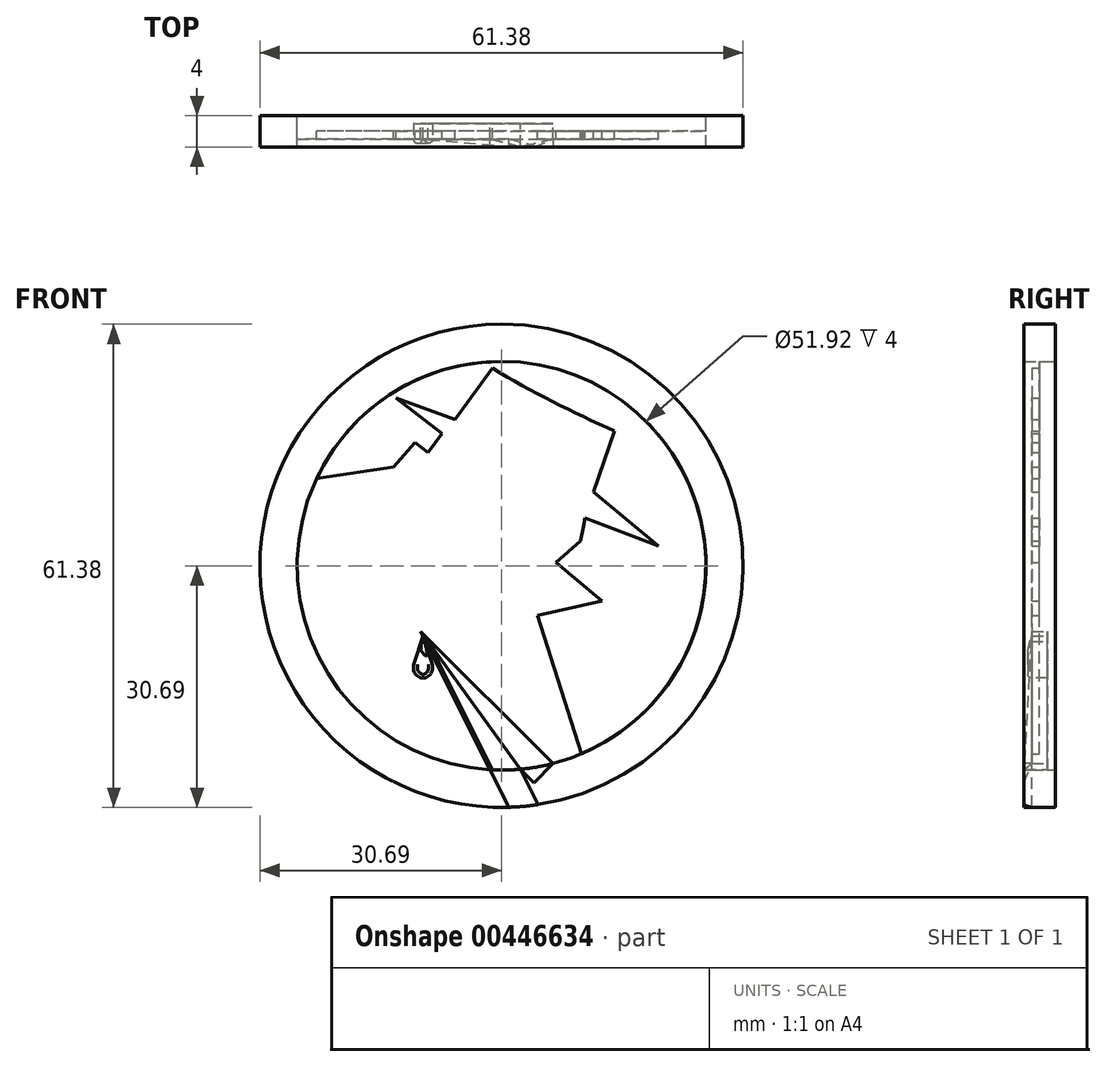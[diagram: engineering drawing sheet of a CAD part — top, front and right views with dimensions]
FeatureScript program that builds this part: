
annotation { "Feature Type Name" : "Feature", "Feature Type Description" : "" }
export const myFeature = defineFeature(function(context is Context, id is Id, definition is map)
    precondition{}
    {
        {
            var Q0;
            Q0=qCreatedBy(makeId("Front.planeOp"),FACE);
            var sketch = newSketch(context, id + "F0", { "sketchPlane" : qUnion([Q0])});
            skLineSegment(sketch, "E0", {"start": v(-50, 0) * mm, "end": v(0, 0) * mm, "construction": true});
            skLineSegment(sketch, "E1", {"start": v(0, 0) * mm, "end": v(50, 0) * mm, "construction": true});
            skCircle(sketch, "E2", {"center": v(-0.5, -1.8) * mm, "radius": 30.7 * mm});
            skCircle(sketch, "E3", {"center": v(-0.5, -1.8) * mm, "radius": 25.96 * mm});
            skLineSegment(sketch, "E4", {"start": v(9.67, -25.69) * mm, "end": v(4.1, -8.1) * mm});
            skLineSegment(sketch, "E5", {"start": v(4.1, -8.1) * mm, "end": v(12.24, -6.27) * mm});
            skLineSegment(sketch, "E6", {"start": v(12.24, -6.27) * mm, "end": v(6.44, -1.37) * mm});
            skLineSegment(sketch, "E7", {"start": v(6.44, -1.37) * mm, "end": v(9.54, 1.38) * mm});
            skLineSegment(sketch, "E8", {"start": v(9.54, 1.38) * mm, "end": v(9.93, 3.2) * mm});
            skLineSegment(sketch, "E9", {"start": v(9.93, 3.2) * mm, "end": v(10.07, 4.26) * mm});
            skLineSegment(sketch, "E10", {"start": v(10.07, 4.26) * mm, "end": v(19.43, 0.68) * mm});
            skLineSegment(sketch, "E11", {"start": v(19.43, 0.68) * mm, "end": v(11.15, 7.54) * mm});
            skLineSegment(sketch, "E12", {"start": v(11.15, 7.54) * mm, "end": v(13.87, 15.33) * mm});
            skLineSegment(sketch, "E13", {"start": v(13.87, 15.33) * mm, "end": v(-1.67, 23.3) * mm, "construction": true});
            skLineSegment(sketch, "E14", {"start": v(-1.67, 23.3) * mm, "end": v(-6.4, 16.78) * mm});
            skLineSegment(sketch, "E15", {"start": v(-6.4, 16.78) * mm, "end": v(-13.93, 19.48) * mm});
            skLineSegment(sketch, "E16", {"start": v(-13.93, 19.48) * mm, "end": v(-8.05, 14.98) * mm});
            skLineSegment(sketch, "E17", {"start": v(-8.05, 14.98) * mm, "end": v(-9.86, 12.61) * mm});
            skLineSegment(sketch, "E18", {"start": v(-9.86, 12.61) * mm, "end": v(-11.49, 13.86) * mm});
            skLineSegment(sketch, "E19", {"start": v(-11.49, 13.86) * mm, "end": v(-14.24, 10.78) * mm});
            skLineSegment(sketch, "E20", {"start": v(-14.24, 10.78) * mm, "end": v(-23.99, 9.26) * mm});
            skArc(sketch, "E21", {"start": v(-1.67, 23.3) * mm, "mid": v(5.97, 19.06) * mm, "end": v(13.87, 15.33) * mm});
            skLineSegment(sketch, "E22", {"start": v(9.99, 3.62) * mm, "end": v(5.75, 4.17) * mm});
            skLineSegment(sketch, "E23", {"start": v(5.75, 4.17) * mm, "end": v(5.75, 1.77) * mm});
            skLineSegment(sketch, "E24", {"start": v(5.75, 1.77) * mm, "end": v(9.86, 2.9) * mm});
            skLineSegment(sketch, "E25", {"start": v(-2.41, 9.54) * mm, "end": v(2.5, 5.2) * mm});
            skLineSegment(sketch, "E26", {"start": v(2.5, 5.2) * mm, "end": v(0.45, 4.05) * mm});
            skLineSegment(sketch, "E27", {"start": v(0.45, 4.05) * mm, "end": v(-2.41, 9.54) * mm});
            skLineSegment(sketch, "E28", {"start": v(6.04, -26.92) * mm, "end": v(-10.78, -10.16) * mm});
            skLineSegment(sketch, "E29", {"start": v(-10.78, -10.16) * mm, "end": v(-1.94, -27.72) * mm});
            skLineSegment(sketch, "E30", {"start": v(1.89, -27.65) * mm, "end": v(-10.78, -10.16) * mm});
            skLineSegment(sketch, "E31", {"start": v(-10.48, -14.68) * mm, "end": v(-10.48, -10.75) * mm, "construction": true});
            skEllipse(sketch, "E32", {"center": v(-10.48, -14.68) * mm, "majorRadius": 1.4 * mm, "minorRadius": 1.23 * mm, "majorAxis": v(0, 1)});
            skLineSegment(sketch, "E33", {"start": v(-11.63, -14.18) * mm, "end": v(-10.48, -10.75) * mm});
            skLineSegment(sketch, "E34", {"start": v(-10.48, -10.75) * mm, "end": v(-9.33, -14.18) * mm});
            skLineSegment(sketch, "E35", {"start": v(-1.65, -27.73) * mm, "end": v(-9.86, -11.42) * mm});
            skLineSegment(sketch, "E36", {"start": v(-1.94, -27.72) * mm, "end": v(7.37, -23.04) * mm, "construction": true});
            skLineSegment(sketch, "E37", {"start": v(6.04, -26.92) * mm, "end": v(-3.22, -36.22) * mm, "construction": true});
            skLineSegment(sketch, "E38", {"start": v(0.6, -25.88) * mm, "end": v(-1.94, -27.72) * mm, "construction": true});
            skLineSegment(sketch, "E39", {"start": v(0.6, -25.88) * mm, "end": v(3.15, -24.04) * mm, "construction": true});
            skSolve(sketch);
        }
        {
            var Q0;
            {var subQ7=sQuery(id+"F0.wireOp",EDGE,"E4");Q0=makeQuery(id+"F0.imprint","IMPRINT",FACE,{"disambiguationData":[TD([[makeQuery(id+"F0.imprint","IMPRINT",EDGE,{"derivedFrom":subQ7}),-1.0]])]});}
            extrude(context, id + "F1", {"entities" : qUnion([Q0]), "depth" : 1 * mm, "offsetDistance" : 25 * mm});
        }
        {
            var Q0;
            {var subQ3=sQuery(id+"F0.wireOp",EDGE,"E4");Q0=makeQuery(id+"F0.imprint","IMPRINT",FACE,{"disambiguationData":[TD([[makeQuery(id+"F0.imprint","IMPRINT",EDGE,{"derivedFrom":subQ3}),1.0]])]});}
            var Q1;
            {var subQ0=sQuery(id+"F0.wireOp",EDGE,"E32");var subQ1=makeQuery(id+"F0.imprint","INTERSECT",VERTEX,{"derivedFrom":[subQ0,sQuery(id+"F0.wireOp",EDGE,"E33")]});Q1=makeQuery(id+"F0.imprint","IMPRINT",FACE,{"disambiguationData":[TD([[makeQuery(id+"F0.imprint","IMPRINT",EDGE,{"disambiguationData":[TD([[subQ1,-1.0]])],"derivedFrom":subQ0}),1.0]])]});}
            var Q2;
            {var subQ0=sQuery(id+"F0.wireOp",EDGE,"E33");Q2=makeQuery(id+"F0.imprint","IMPRINT",FACE,{"disambiguationData":[TD([[makeQuery(id+"F0.imprint","IMPRINT",EDGE,{"derivedFrom":subQ0}),-1.0]])]});}
            extrude(context, id + "F2", {"entities" : qUnion([Q0, Q1, Q2]), "depth" : 2 * mm, "offsetDistance" : 25 * mm});
        }
        {
            var Q0;
            {var subQ7=sQuery(id+"F0.wireOp",EDGE,"E4");Q0=makeQuery(id+"F0.imprint","IMPRINT",FACE,{"disambiguationData":[TD([[makeQuery(id+"F0.imprint","IMPRINT",EDGE,{"derivedFrom":subQ7}),-1.0]])]});}
            var Q1;
            {var subQ3=sQuery(id+"F0.wireOp",EDGE,"E4");Q1=makeQuery(id+"F0.imprint","IMPRINT",FACE,{"disambiguationData":[TD([[makeQuery(id+"F0.imprint","IMPRINT",EDGE,{"derivedFrom":subQ3}),1.0]])]});}
            var Q2;
            {var subQ0=sQuery(id+"F0.wireOp",EDGE,"E28");Q2=makeQuery(id+"F0.imprint","IMPRINT",FACE,{"disambiguationData":[TD([[makeQuery(id+"F0.imprint","IMPRINT",EDGE,{"derivedFrom":subQ0}),1.0]])]});}
            var Q3;
            {var subQ3=sQuery(id+"F0.wireOp",EDGE,"E30");Q3=makeQuery(id+"F0.imprint","IMPRINT",FACE,{"disambiguationData":[TD([[makeQuery(id+"F0.imprint","IMPRINT",EDGE,{"derivedFrom":subQ3}),1.0]])]});}
            var Q4;
            {var subQ0=sQuery(id+"F0.wireOp",EDGE,"E33");Q4=makeQuery(id+"F0.imprint","IMPRINT",FACE,{"disambiguationData":[TD([[makeQuery(id+"F0.imprint","IMPRINT",EDGE,{"derivedFrom":subQ0}),-1.0]])]});}
            var Q5;
            {var subQ0=sQuery(id+"F0.wireOp",EDGE,"E32");var subQ1=makeQuery(id+"F0.imprint","INTERSECT",VERTEX,{"derivedFrom":[subQ0,sQuery(id+"F0.wireOp",EDGE,"E33")]});Q5=makeQuery(id+"F0.imprint","IMPRINT",FACE,{"disambiguationData":[TD([[makeQuery(id+"F0.imprint","IMPRINT",EDGE,{"disambiguationData":[TD([[subQ1,-1.0]])],"derivedFrom":subQ0}),1.0]])]});}
            var Q6;
            Q6=makeQuery(id+"F0.imprint","IMPRINT",FACE,{"disambiguationData":[TD([[makeQuery(id+"F0.imprint","IMPRINT",EDGE,{"derivedFrom":sQuery(id+"F0.wireOp",EDGE,"E25")}),-1.0]])]});
            var Q7;
            {var subQ0=sQuery(id+"F0.wireOp",EDGE,"E22");Q7=makeQuery(id+"F0.imprint","IMPRINT",FACE,{"disambiguationData":[TD([[makeQuery(id+"F0.imprint","IMPRINT",EDGE,{"derivedFrom":subQ0}),1.0]])]});}
            var Q8;
            {var subQ3=sQuery(id+"F0.wireOp",EDGE,"E35");Q8=makeQuery(id+"F0.imprint","IMPRINT",FACE,{"disambiguationData":[TD([[makeQuery(id+"F0.imprint","IMPRINT",EDGE,{"derivedFrom":subQ3}),1.0]])]});}
            extrude(context, id + "F3", {"entities" : qUnion([Q0, Q1, Q2, Q3, Q4, Q5, Q6, Q7, Q8]), "operationType" : NewBodyOperationType.ADD, "oppositeDirection" : true, "depth" : 1 * mm, "offsetDistance" : 25 * mm});
        }
        {
            var Q0;
            Q0=makeQuery(id+"F0.imprint","IMPRINT",FACE,{"disambiguationData":[TD([[makeQuery(id+"F0.imprint","IMPRINT",EDGE,{"derivedFrom":sQuery(id+"F0.wireOp",EDGE,"E25")}),-1.0]])]});
            var Q1;
            {var subQ0=sQuery(id+"F0.wireOp",EDGE,"E22");Q1=makeQuery(id+"F0.imprint","IMPRINT",FACE,{"disambiguationData":[TD([[makeQuery(id+"F0.imprint","IMPRINT",EDGE,{"derivedFrom":subQ0}),1.0]])]});}
            extrude(context, id + "F4", {"entities" : qUnion([Q0, Q1]), "operationType" : NewBodyOperationType.ADD, "depth" : 2 * mm, "offsetDistance" : 25 * mm});
        }
        {
            var Q0;
            Q0=makeQuery(id+"F0.imprint","IMPRINT",FACE,{"disambiguationData":[TD([[makeQuery(id+"F0.imprint","IMPRINT",EDGE,{"derivedFrom":sQuery(id+"F0.wireOp",EDGE,"E2")}),1.0]])]});
            extrude(context, id + "F5", {"entities" : qUnion([Q0]), "endBound" : BoundingType.SYMMETRIC, "depth" : 6 * mm, "offsetDistance" : 25 * mm});
        }
        {
            var Q0;
            {var subQ0=sQuery(id+"F0.wireOp",EDGE,"E33");Q0=makeQuery(id+"F0.imprint","IMPRINT",FACE,{"disambiguationData":[TD([[makeQuery(id+"F0.imprint","IMPRINT",EDGE,{"derivedFrom":subQ0}),-1.0]])]});}
            var Q1;
            {var subQ0=sQuery(id+"F0.wireOp",EDGE,"E32");var subQ1=makeQuery(id+"F0.imprint","INTERSECT",VERTEX,{"derivedFrom":[subQ0,sQuery(id+"F0.wireOp",EDGE,"E33")]});Q1=makeQuery(id+"F0.imprint","IMPRINT",FACE,{"disambiguationData":[TD([[makeQuery(id+"F0.imprint","IMPRINT",EDGE,{"disambiguationData":[TD([[subQ1,-1.0]])],"derivedFrom":subQ0}),1.0]])]});}
            extrude(context, id + "F6", {"entities" : qUnion([Q0, Q1]), "depth" : 2.5 * mm, "offsetDistance" : 25 * mm});
        }
        {
            var Q0;
            Q0=makeQuery(id+"F6.opExtrude","CAP_FACE",FACE,{"disambiguationData":[OSD([sQuery(id+"F0.wireOp",EDGE,"E32"),sQuery(id+"F0.wireOp",EDGE,"E33"),sQuery(id+"F0.wireOp",EDGE,"E34")])],"isStart":false});
            fillet(context, id + "F7", {"entities" : qUnion([Q0]), "radius" : .5 * mm, "tangentPropagation" : true, "allowEdgeOverflow" : false});
        }
        {
            var Q0;
            {var subQ3=sQuery(id+"F0.wireOp",EDGE,"E30");Q0=makeQuery(id+"F0.imprint","IMPRINT",FACE,{"disambiguationData":[TD([[makeQuery(id+"F0.imprint","IMPRINT",EDGE,{"derivedFrom":subQ3}),1.0]])]});}
            extrude(context, id + "F8", {"entities" : qUnion([Q0]), "depth" : 3 * mm, "offsetDistance" : 25 * mm});
        }
        {
            var Q0;
            {var subQ0=sQuery(id+"F0.wireOp",EDGE,"E28");Q0=makeQuery(id+"F0.imprint","IMPRINT",FACE,{"disambiguationData":[TD([[makeQuery(id+"F0.imprint","IMPRINT",EDGE,{"derivedFrom":subQ0}),1.0]])]});}
            var Q1;
            {var subQ3=sQuery(id+"F0.wireOp",EDGE,"E35");Q1=makeQuery(id+"F0.imprint","IMPRINT",FACE,{"disambiguationData":[TD([[makeQuery(id+"F0.imprint","IMPRINT",EDGE,{"derivedFrom":subQ3}),1.0]])]});}
            extrude(context, id + "F9", {"entities" : qUnion([Q0, Q1]), "depth" : 3 * mm, "offsetDistance" : 25 * mm});
        }
        {
            var Q0;
            Q0=sQuery(id+"F0.wireOp",EDGE,"E36");
            var Q1;
            Q1=qCreatedBy(makeId("Front.planeOp"),FACE);
            cPlane(context, id + "F10", {"entities" : qUnion([Q0, Q1]), "cplaneType" : CPlaneType.LINE_ANGLE, "offset" : 25 * mm, "angle" : 90 * degree, "width" : 150 * mm, "height" : 150 * mm});
        }
        {
            var Q0;
            Q0=qCreatedBy(id+"F10.planeOp",FACE);
            var sketch = newSketch(context, id + "F11", { "sketchPlane" : qUnion([Q0])});
            skLineSegment(sketch, "E40.0", {"start": v(-14.2, -3) * mm, "end": v(-14.2, 0) * mm, "construction": true});
            skLineSegment(sketch, "E41.0", {"start": v(-10.74, -3) * mm, "end": v(-10.74, 0) * mm, "construction": true});
            skLineSegment(sketch, "E42", {"start": v(-10.74, -3) * mm, "end": v(-14.2, -2) * mm});
            skLineSegment(sketch, "E43", {"start": v(-14.2, -2) * mm, "end": v(-14.2, -4.14) * mm});
            skLineSegment(sketch, "E44", {"start": v(-14.2, -4.14) * mm, "end": v(-10.74, -3) * mm});
            skSolve(sketch);
        }
        {
            var Q0;
            Q0=sQuery(id+"F0.wireOp",EDGE,"E37");
            var Q1;
            Q1=qCreatedBy(makeId("Front.planeOp"),FACE);
            cPlane(context, id + "F12", {"entities" : qUnion([Q0, Q1]), "cplaneType" : CPlaneType.LINE_ANGLE, "offset" : 25 * mm, "angle" : 90 * degree, "width" : 150 * mm, "height" : 150 * mm});
        }
        {
            var Q0;
            Q0=qCreatedBy(id+"F12.planeOp",FACE);
            var sketch = newSketch(context, id + "F13", { "sketchPlane" : qUnion([Q0])});
            skLineSegment(sketch, "E45.0", {"start": v(-3, -18.25) * mm, "end": v(0, -18.25) * mm, "construction": true});
            skLineSegment(sketch, "E46.0", {"start": v(-3, -14.8) * mm, "end": v(0, -14.8) * mm, "construction": true});
            skLineSegment(sketch, "E47", {"start": v(-3, -18.25) * mm, "end": v(-2, -14.8) * mm});
            skLineSegment(sketch, "E48", {"start": v(-2, -14.8) * mm, "end": v(-6.2, -14.8) * mm});
            skLineSegment(sketch, "E49", {"start": v(-6.2, -14.8) * mm, "end": v(-3, -18.25) * mm});
            skSolve(sketch);
        }
        {
            var Q0;
            Q0=makeQuery(id+"F11.imprint","IMPRINT",FACE,{"disambiguationData":[TD([[makeQuery(id+"F11.imprint","IMPRINT",EDGE,{"derivedFrom":sQuery(id+"F11.wireOp",EDGE,"E42")}),1.0]])]});
            extrude(context, id + "F14", {"entities" : qUnion([Q0]), "operationType" : NewBodyOperationType.REMOVE, "endBound" : BoundingType.SYMMETRIC, "oppositeDirection" : true, "depth" : 40 * mm, "offsetDistance" : 25 * mm});
        }
        {
            var Q0;
            Q0=makeQuery(id+"F13.imprint","IMPRINT",FACE,{"disambiguationData":[TD([[makeQuery(id+"F13.imprint","IMPRINT",EDGE,{"derivedFrom":sQuery(id+"F13.wireOp",EDGE,"E47")}),1.0]])]});
            extrude(context, id + "F15", {"entities" : qUnion([Q0]), "operationType" : NewBodyOperationType.REMOVE, "oppositeDirection" : true, "depth" : 25 * mm, "offsetDistance" : 25 * mm});
        }
        {
            var Q0;
            Q0=qCreatedBy(makeId("Top.planeOp"),FACE);
            var sketch = newSketch(context, id + "F16", { "sketchPlane" : qUnion([Q0])});
            skLineSegment(sketch, "E50.bottom", {"start": v(32.73, 4.97) * mm, "end": v(-32.74, 4.97) * mm});
            skLineSegment(sketch, "E50.top", {"start": v(32.73, 1) * mm, "end": v(-32.74, 1) * mm});
            skLineSegment(sketch, "E50.left", {"start": v(32.73, 4.97) * mm, "end": v(32.73, 1) * mm});
            skLineSegment(sketch, "E50.right", {"start": v(-32.74, 4.97) * mm, "end": v(-32.74, 1) * mm});
            skSolve(sketch);
        }
        {
            var Q0;
            Q0=makeQuery(id+"F16.imprint","IMPRINT",FACE,{"disambiguationData":[TD([[makeQuery(id+"F16.imprint","IMPRINT",EDGE,{"derivedFrom":sQuery(id+"F16.wireOp",EDGE,"E50.bottom")}),1.0]])]});
            extrude(context, id + "F17", {"entities" : qUnion([Q0]), "operationType" : NewBodyOperationType.REMOVE, "endBound" : BoundingType.SYMMETRIC, "oppositeDirection" : true, "depth" : 100 * mm, "offsetDistance" : 25 * mm});
        }
    });
